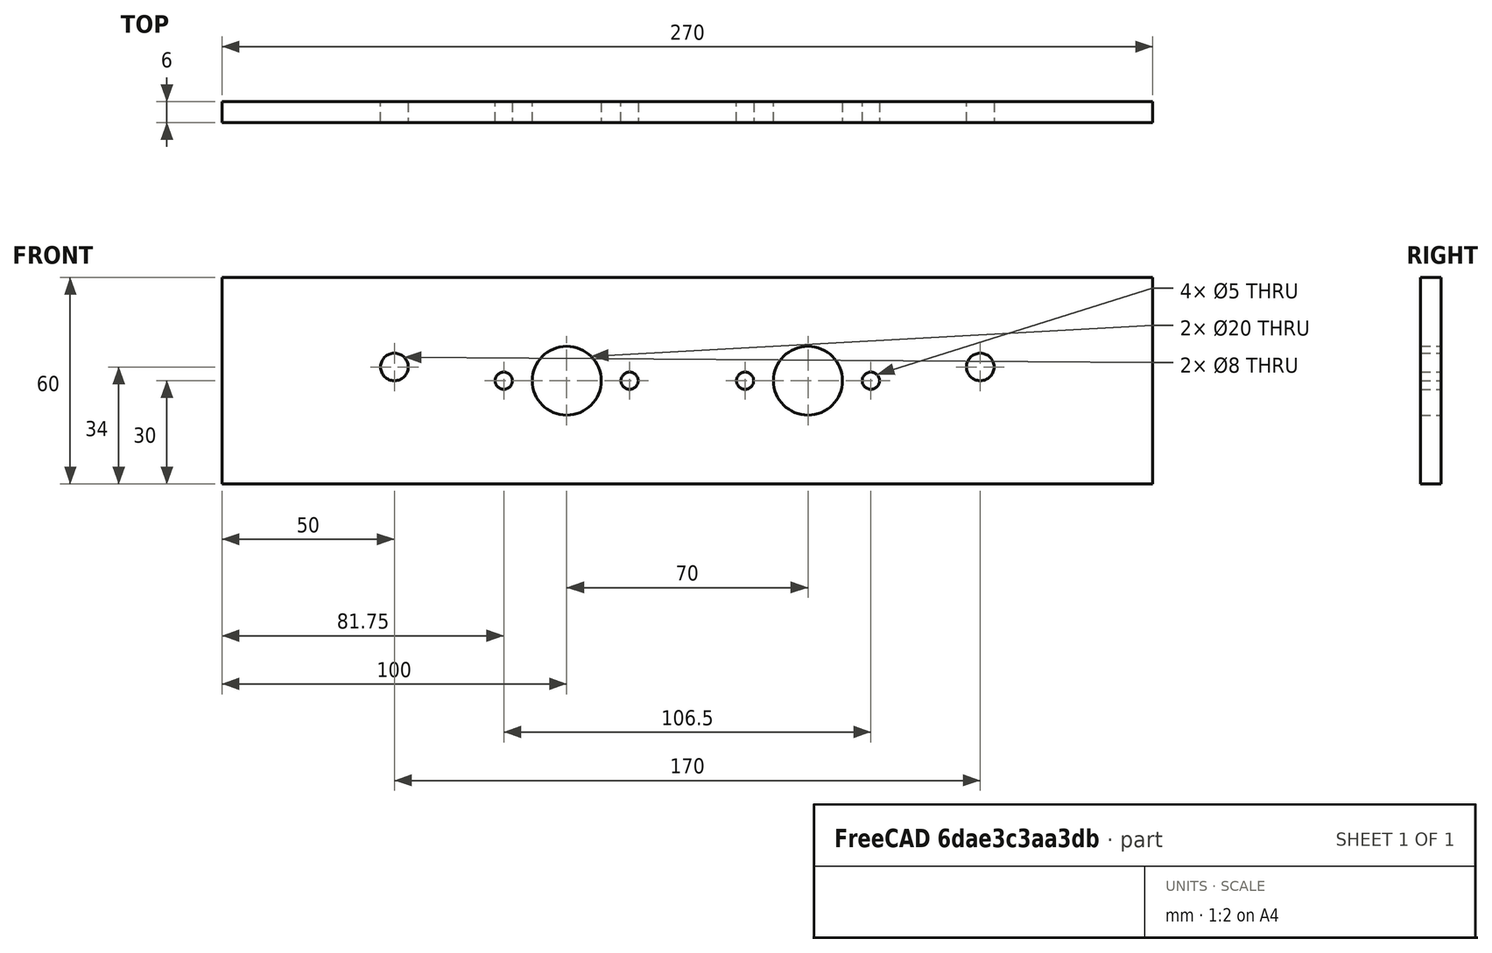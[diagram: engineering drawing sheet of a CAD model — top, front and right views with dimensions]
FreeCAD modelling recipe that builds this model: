
FCSTD DOCUMENT  (FreeCAD 0.18R4 (GitTag))
Label: soporte_rod1
License: All rights reserved
LicenseURL: http://en.wikipedia.org/wiki/All_rights_reserved
objects: Sketcher::SketchObject×1, PartDesign::Pad×1, PartDesign::Body×1
note: 4 computed .brp shape members not serialized (recipe doc carries the construction recipe); baked Part::Feature solids carry a one-line shape summary decoded from their .brp

FEATURE [Sketcher::SketchObject] Sketch
  MapMode = 5
  Placement = pos=(0,0,0) rot=(1,0,0;1.5708rad)
  Support = -> [XZ_Plane]
  sketch-geometry (12):
    g0: LineSegment StartX=0 StartY=0 StartZ=0 EndX=270 EndY=0 EndZ=0
    g1: LineSegment StartX=270 StartY=0 StartZ=0 EndX=270 EndY=60 EndZ=0
    g2: LineSegment StartX=270 StartY=60 StartZ=0 EndX=0 EndY=60 EndZ=0
    g3: LineSegment StartX=0 StartY=60 StartZ=0 EndX=0 EndY=0 EndZ=0
    g4: Circle CenterX=100 CenterY=30 CenterZ=0 NormalX=0 NormalY=0 NormalZ=1 AngleXU=0 Radius=10
    g5: Circle CenterX=170 CenterY=30 CenterZ=0 NormalX=0 NormalY=0 NormalZ=1 AngleXU=0 Radius=10
    g6: Circle CenterX=81.75 CenterY=30 CenterZ=0 NormalX=0 NormalY=0 NormalZ=1 AngleXU=0 Radius=2.5
    g7: Circle CenterX=118.25 CenterY=30 CenterZ=0 NormalX=0 NormalY=0 NormalZ=1 AngleXU=0 Radius=2.5
    g8: Circle CenterX=151.75 CenterY=30 CenterZ=0 NormalX=0 NormalY=0 NormalZ=1 AngleXU=0 Radius=2.5
    g9: Circle CenterX=188.25 CenterY=30 CenterZ=0 NormalX=0 NormalY=0 NormalZ=1 AngleXU=0 Radius=2.5
    g10: Circle CenterX=50 CenterY=34 CenterZ=0 NormalX=0 NormalY=0 NormalZ=1 AngleXU=0 Radius=4
    g11: Circle CenterX=220 CenterY=34 CenterZ=0 NormalX=0 NormalY=0 NormalZ=1 AngleXU=0 Radius=4
  constraints (35):
    c: Coincident(g0,g1)
    c: Coincident(g1,g2)
    c: Coincident(g2,g3)
    c: Coincident(g3,g0)
    c: Horizontal(g0)
    c: Horizontal(g2)
    c: Vertical(g1)
    c: Vertical(g3)
    c: Coincident(g0,g-1)
    c: DistanceX(g0,g0) = 270
    c: DistanceY(g3,g3) = 60
    c: Distance(g4,g2) = 30
    c: Distance(g4,g3) = 100
    c: Radius(g4) = 10
    c: Equal(g4,g5) = 6
    c: Distance(g5,g3) = 170
    c: Distance(g5,g2) = 30
    c: Equal(g6,g7)
    c: Equal(g7,g8)
    c: Equal(g8,g9)
    c: Radius(g6) = 2.5
    c: Distance(g6,g7) = 36.5
    c: Distance(g8,g9) = 36.5
    c: Distance(g6,g2) = 30
    c: Distance(g7,g2) = 30
    c: Distance(g8,g2) = 30
    c: Distance(g9,g2) = 30
    c: Distance(g7,g4) = 18.25
    c: Distance(g5,g9) = 18.25
    c: Equal(g10,g11)
    c: Radius(g11) = 4
    c: Distance(g10,g2) = 26
    c: Distance(g10,g11) = 170
    c: Distance(g11,g2) = 26
    c: Distance(g10,g3) = 50
FEATURE [PartDesign::Pad] Pad
  Length = 6
  Length2 = 100
  Placement = pos=(0,0,0) rot=(1,0,0;1.5708rad)
  Profile = -> Sketch
  Type = 0
FEATURE [PartDesign::Body] Body
  Group = -> [Sketch,Pad]
  Origin = -> Origin
  Tip = -> Pad
